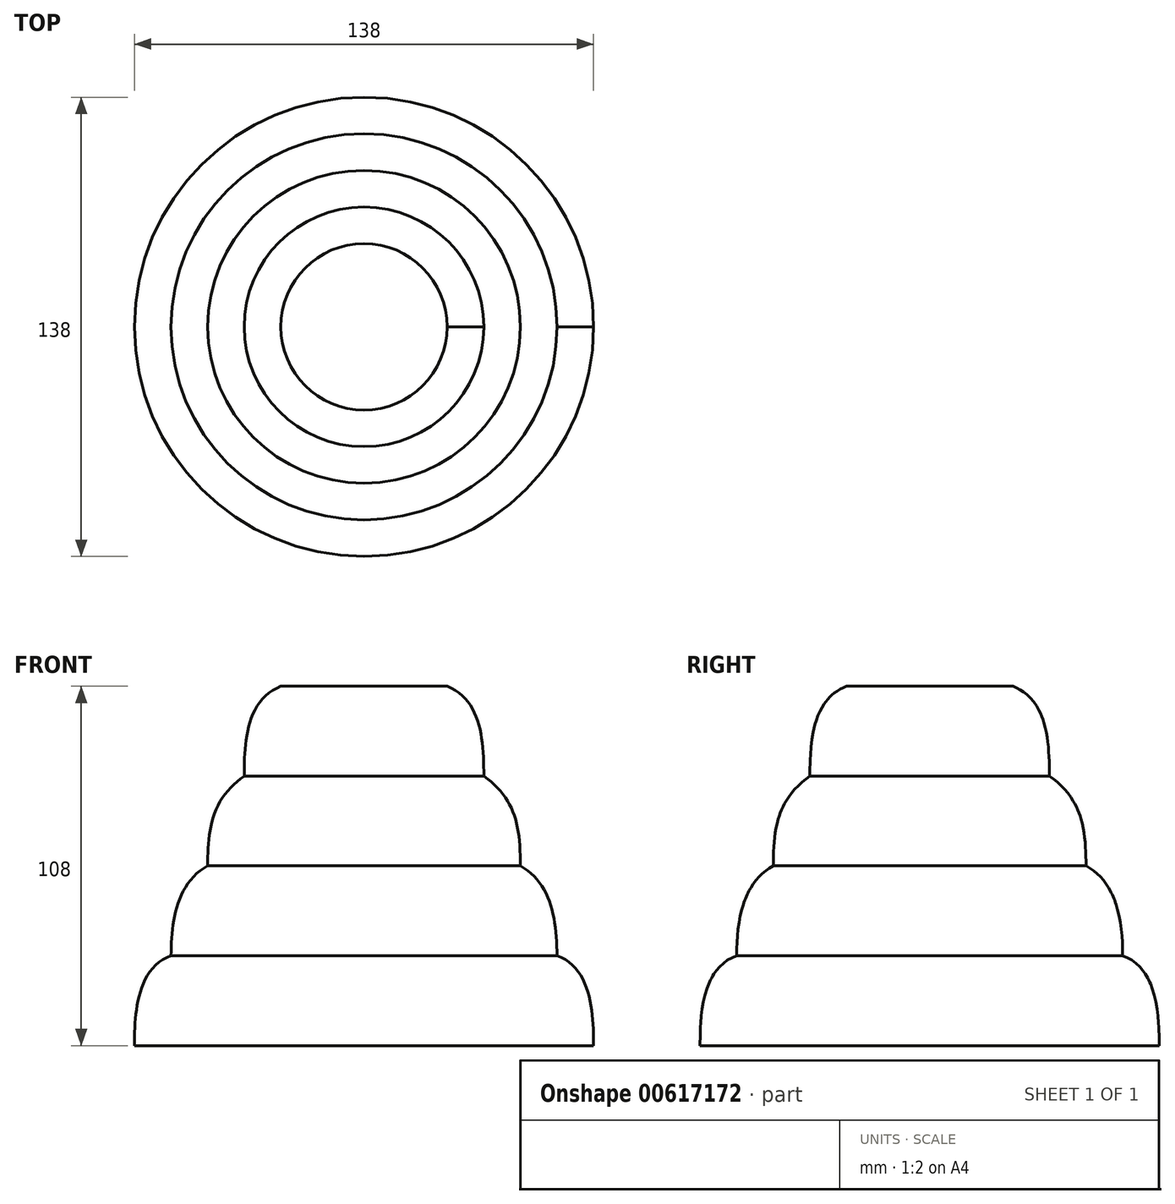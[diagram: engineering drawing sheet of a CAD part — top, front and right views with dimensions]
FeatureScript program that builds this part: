
annotation { "Feature Type Name" : "Feature", "Feature Type Description" : "" }
export const myFeature = defineFeature(function(context is Context, id is Id, definition is map)
    precondition{}
    {
        {
            var Q0;
            Q0=qCreatedBy(makeId("Front.planeOp"),FACE);
            var sketch = newSketch(context, id + "F0", { "sketchPlane" : qUnion([Q0])});
            skLineSegment(sketch, "E0", {"start": v(0, 54) * mm, "end": v(0, -54) * mm});
            skLineSegment(sketch, "E1", {"start": v(0, -54) * mm, "end": v(-69, -54) * mm});
            skFitSpline(sketch, "E2", {"points": [v(-36, 27) * mm, v(-25, 54) * mm], "startDerivative": vector(0.05, 32.59) * mm, "endDerivative": vector(30.76, 12.47) * mm});
            skFitSpline(sketch, "E3", {"points": [v(-36, 27) * mm, v(-47, 0) * mm], "startDerivative": vector(-27.57, -19.55) * mm, "endDerivative": vector(0, -37.37) * mm});
            skFitSpline(sketch, "E4", {"points": [v(-47, 0) * mm, v(-58, -27) * mm], "startDerivative": vector(-27.2, -14.72) * mm, "endDerivative": vector(0, -32.78) * mm});
            skFitSpline(sketch, "E5", {"points": [v(-58, -27) * mm, v(-69, -54) * mm], "startDerivative": vector(-31.54, -10.93) * mm, "endDerivative": vector(0, -26.66) * mm});
            skLineSegment(sketch, "E6", {"start": v(-25, 54) * mm, "end": v(0, 54) * mm});
            skSolve(sketch);
        }
        {
            var Q0;
            Q0=qCreatedBy(makeId("Front.planeOp"),FACE);
            var sketch = newSketch(context, id + "F1", { "sketchPlane" : qUnion([Q0])});
            skLineSegment(sketch, "E7", {"start": v(0, 62.62) * mm, "end": v(0, -62.62) * mm});
            skSolve(sketch);
        }
        {
            var Q0;
            Q0=makeQuery(id+"F0.imprint","IMPRINT",FACE,{"disambiguationData":[TD([[makeQuery(id+"F0.imprint","IMPRINT",EDGE,{"derivedFrom":sQuery(id+"F0.wireOp",EDGE,"E0")}),-1.0]])]});
            var Q1;
            Q1=sQuery(id+"F1.wireOp",EDGE,"E7");
            revolve(context, id + "F2", {"entities" : qUnion([Q0]), "axis" : qUnion([Q1]), "revolveType" : RevolveType.FULL});
        }
    });
